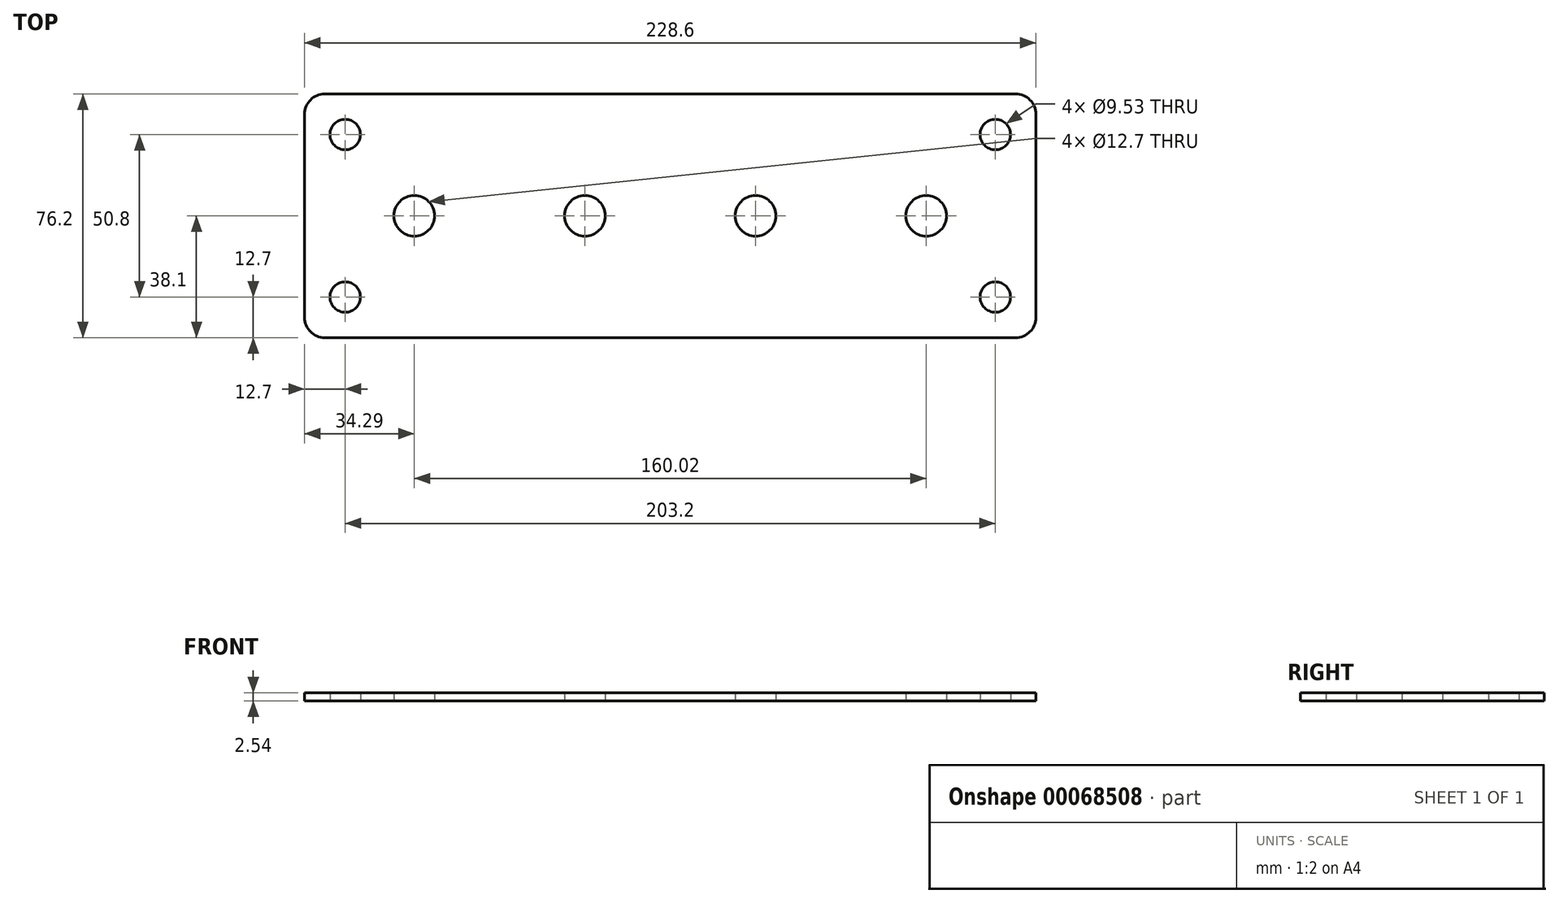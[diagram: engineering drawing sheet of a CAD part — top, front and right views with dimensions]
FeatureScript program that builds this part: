
annotation { "Feature Type Name" : "Feature", "Feature Type Description" : "" }
export const myFeature = defineFeature(function(context is Context, id is Id, definition is map)
    precondition{}
    {
        {
            var Q0;
            Q0=qCreatedBy(makeId("Top.planeOp"),FACE);
            var sketch = newSketch(context, id + "F0", { "sketchPlane" : qUnion([Q0])});
            skLineSegment(sketch, "E0.bottom", {"start": v(-107.95, 38.1) * mm, "end": v(107.95, 38.1) * mm});
            skLineSegment(sketch, "E0.top", {"start": v(-107.95, -38.1) * mm, "end": v(107.95, -38.1) * mm});
            skLineSegment(sketch, "E0.left", {"start": v(-114.3, 31.75) * mm, "end": v(-114.3, -31.75) * mm});
            skLineSegment(sketch, "E0.right", {"start": v(114.3, 31.75) * mm, "end": v(114.3, -31.75) * mm});
            skLineSegment(sketch, "E1", {"start": v(0, 38.1) * mm, "end": v(0, 0) * mm, "construction": true});
            skLineSegment(sketch, "E2", {"start": v(0, 0) * mm, "end": v(-114.3, 0) * mm, "construction": true});
            skCircle(sketch, "E3", {"center": v(101.6, 25.4) * mm, "radius": 4.76 * mm});
            skCircle(sketch, "E4.MirrorC", {"center": v(101.6, -25.4) * mm, "radius": 4.76 * mm});
            skCircle(sketch, "E5.MirrorC", {"center": v(-101.6, 25.4) * mm, "radius": 4.76 * mm});
            skCircle(sketch, "E6.MirrorC", {"center": v(-101.6, -25.4) * mm, "radius": 4.76 * mm});
            skCircle(sketch, "E7", {"center": v(-80, 0) * mm, "radius": 6.35 * mm});
            skCircle(sketch, "E8.1.0.0", {"center": v(-26.67, 0) * mm, "radius": 6.35 * mm});
            skCircle(sketch, "E8.2.0.0", {"center": v(26.67, 0) * mm, "radius": 6.35 * mm});
            skLineSegment(sketch, "E8.direction1", {"start": v(-80, 0) * mm, "end": v(-26.67, 0) * mm, "construction": true});
            skPoint(sketch, "E9.visualSharp", {"position": v(-114.3, 38.1) * mm});
            skArc(sketch, "E9.filletArc", {"start": v(-107.95, 38.1) * mm, "mid": v(-112.44, 36.24) * mm, "end": v(-114.3, 31.75) * mm});
            skPoint(sketch, "E10.visualSharp", {"position": v(114.3, 38.1) * mm});
            skArc(sketch, "E10.filletArc", {"start": v(114.3, 31.75) * mm, "mid": v(112.44, 36.24) * mm, "end": v(107.95, 38.1) * mm});
            skPoint(sketch, "E11.visualSharp", {"position": v(114.3, -38.1) * mm});
            skArc(sketch, "E11.filletArc", {"start": v(107.95, -38.1) * mm, "mid": v(112.44, -36.24) * mm, "end": v(114.3, -31.75) * mm});
            skPoint(sketch, "E12.visualSharp", {"position": v(-114.3, -38.1) * mm});
            skArc(sketch, "E12.filletArc", {"start": v(-114.3, -31.75) * mm, "mid": v(-112.44, -36.24) * mm, "end": v(-107.95, -38.1) * mm});
            skCircle(sketch, "E13.0.3.0", {"center": v(80, 0) * mm, "radius": 6.35 * mm});
            skSolve(sketch);
        }
        {
            var Q0;
            Q0=makeQuery(id+"F0.imprint","IMPRINT",FACE,{"disambiguationData":[TD([[makeQuery(id+"F0.imprint","IMPRINT",EDGE,{"derivedFrom":sQuery(id+"F0.wireOp",EDGE,"E0.bottom")}),-1.0]])]});
            extrude(context, id + "F1", {"entities" : qUnion([Q0]), "depth" : 2.54 * mm, "offsetDistance" : 25.4 * mm});
        }
    });
